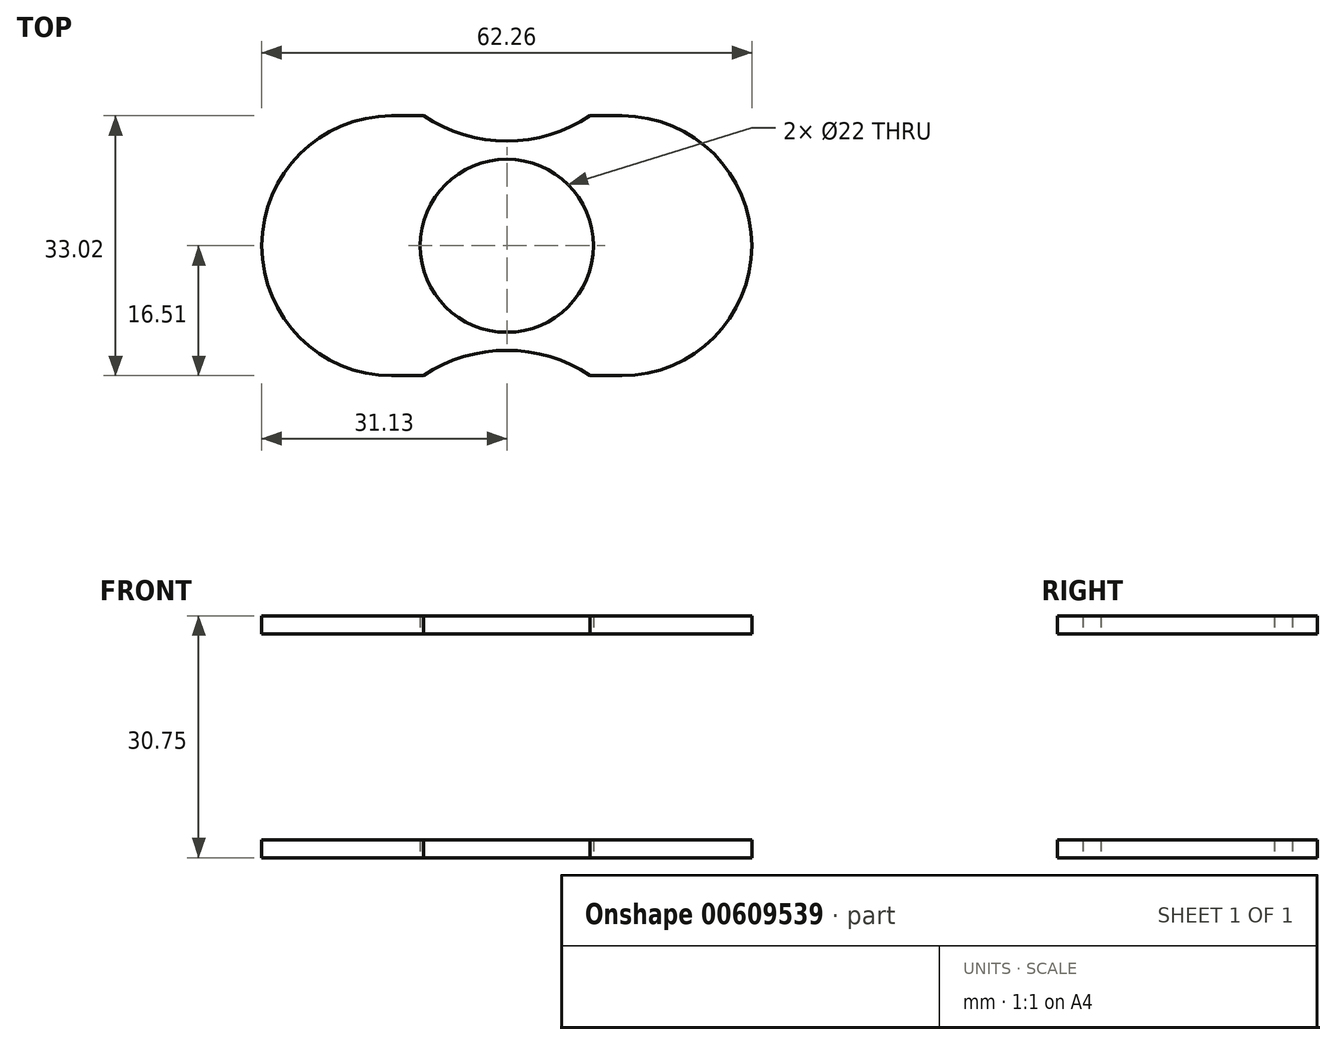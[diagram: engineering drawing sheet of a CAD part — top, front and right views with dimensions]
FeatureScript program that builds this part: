
annotation { "Feature Type Name" : "Feature", "Feature Type Description" : "" }
export const myFeature = defineFeature(function(context is Context, id is Id, definition is map)
    precondition{}
    {
        {
            var Q0;
            Q0=qCreatedBy(makeId("Top.planeOp"),FACE);
            var sketch = newSketch(context, id + "F0", { "sketchPlane" : qUnion([Q0])});
            skLineSegment(sketch, "E0.bottom", {"start": v(27.94, 16.51) * mm, "end": v(-27.94, 16.51) * mm});
            skLineSegment(sketch, "E0.top", {"start": v(27.94, -16.5) * mm, "end": v(-27.94, -16.5) * mm});
            skLineSegment(sketch, "E0.left", {"start": v(27.94, 16.51) * mm, "end": v(27.94, -16.5) * mm});
            skLineSegment(sketch, "E0.right", {"start": v(-27.94, 16.51) * mm, "end": v(-27.94, -16.5) * mm});
            skPoint(sketch, "E0.middle", {"position": v(0, 0) * mm});
            skLineSegment(sketch, "E1", {"start": v(0, 0) * mm, "end": v(0, 32.3) * mm});
            skPoint(sketch, "E1.endSnap0", {"position": v(0, 16.51) * mm});
            skCircle(sketch, "E2", {"center": v(0, 32.3) * mm, "radius": 19 * mm});
            skCircle(sketch, "E3.MirrorC", {"center": v(0, -32.3) * mm, "radius": 19 * mm});
            skLineSegment(sketch, "E4.MirrorCS", {"start": v(0, 0) * mm, "end": v(0, -32.3) * mm});
            skCircle(sketch, "E5", {"center": v(0, 0) * mm, "radius": 11 * mm});
            skArc(sketch, "E6", {"start": v(-14.62, 16.51) * mm, "mid": v(-31.13, 0) * mm, "end": v(-14.62, -16.5) * mm});
            skArc(sketch, "E7.MirrorCS", {"start": v(14.62, 16.51) * mm, "mid": v(31.13, 0) * mm, "end": v(14.62, -16.5) * mm});
            skSolve(sketch);
        }
        {
            var Q0;
            {var subQ13=sQuery(id+"F0.wireOp",EDGE,"b0117b07-4221-4cab-a59d-326007b296140.MirrorCS");Q0=makeQuery(id+"F0.imprint","IMPRINT",FACE,{"disambiguationData":[TD([[makeQuery(id+"F0.imprint","IMPRINT",EDGE,{"derivedFrom":subQ13}),-1.0]])]});}
            var Q1;
            {var subQ0=sQuery(id+"F0.wireOp",EDGE,"6c8b0966-cea6-4925-859d-a13cfbc1d1b40.MirrorCS");Q1=makeQuery(id+"F0.imprint","IMPRINT",FACE,{"disambiguationData":[TD([[makeQuery(id+"F0.imprint","IMPRINT",EDGE,{"derivedFrom":subQ0}),-1.0]])]});}
            var Q2;
            {var subQ0=sQuery(id+"F0.wireOp",EDGE,"xIR9I51y-JtoL-diQV-116K-h4xmKDdJz4Ub");Q2=makeQuery(id+"F0.imprint","IMPRINT",FACE,{"disambiguationData":[TD([[makeQuery(id+"F0.imprint","IMPRINT",EDGE,{"derivedFrom":subQ0}),1.0]])]});}
            var Q3;
            {var subQ0=sQuery(id+"F0.wireOp",EDGE,"UGArh95A-ruyk-S8bi-ieUh-TaEx0mV84ndZ");Q3=makeQuery(id+"F0.imprint","IMPRINT",FACE,{"disambiguationData":[TD([[makeQuery(id+"F0.imprint","IMPRINT",EDGE,{"derivedFrom":subQ0}),-1.0]])]});}
            var Q4;
            {var subQ0=sQuery(id+"F0.wireOp",EDGE,"feb42550-40b8-4ec1-8f83-4ec7968d60970.MirrorCS");Q4=makeQuery(id+"F0.imprint","IMPRINT",FACE,{"disambiguationData":[TD([[makeQuery(id+"F0.imprint","IMPRINT",EDGE,{"derivedFrom":subQ0}),-1.0]])]});}
            var Q5;
            {var subQ0=sQuery(id+"F0.wireOp",EDGE,"6c8b0966-cea6-4925-859d-a13cfbc1d1b40.MirrorCS");Q5=makeQuery(id+"F0.imprint","IMPRINT",FACE,{"disambiguationData":[TD([[makeQuery(id+"F0.imprint","IMPRINT",EDGE,{"derivedFrom":subQ0}),1.0]])]});}
            var Q6;
            {var subQ0=sQuery(id+"F0.wireOp",EDGE,"E6");var subQ9=sQuery(id+"F0.wireOp",EDGE,"E0.bottom");var subQ13=makeQuery(id+"F0.imprint","INTERSECT",VERTEX,{"derivedFrom":[subQ9,subQ0]});Q6=makeQuery(id+"F0.imprint","IMPRINT",FACE,{"disambiguationData":[TD([[makeQuery(id+"F0.imprint","IMPRINT",EDGE,{"disambiguationData":[TD([[subQ13,1.0]])],"derivedFrom":subQ9}),1.0]])]});}
            var Q7;
            {var subQ5=sQuery(id+"F0.wireOp",EDGE,"E7.MirrorCS");var subQ9=sQuery(id+"F0.wireOp",EDGE,"E0.bottom");var subQ10=makeQuery(id+"F0.imprint","INTERSECT",VERTEX,{"derivedFrom":[subQ9,subQ5]});Q7=makeQuery(id+"F0.imprint","IMPRINT",FACE,{"disambiguationData":[TD([[makeQuery(id+"F0.imprint","IMPRINT",EDGE,{"disambiguationData":[TD([[subQ10,-1.0]])],"derivedFrom":subQ9}),1.0]])]});}
            var Q8;
            {var subQ0=sQuery(id+"F0.wireOp",EDGE,"E7.MirrorCS");var subQ1=sQuery(id+"F0.wireOp",EDGE,"E0.left");var subQ2=makeQuery(id+"F0.imprint","INTERSECT",VERTEX,{"disambiguationData":[OD(0.0)],"derivedFrom":[subQ1,subQ0]});Q8=makeQuery(id+"F0.imprint","IMPRINT",FACE,{"disambiguationData":[TD([[makeQuery(id+"F0.imprint","IMPRINT",EDGE,{"disambiguationData":[TD([[subQ2,-1.0]])],"derivedFrom":subQ1}),1.0]])]});}
            var Q9;
            {var subQ0=sQuery(id+"F0.wireOp",EDGE,"E6");var subQ1=sQuery(id+"F0.wireOp",EDGE,"E0.right");var subQ2=makeQuery(id+"F0.imprint","INTERSECT",VERTEX,{"disambiguationData":[OD(0.0)],"derivedFrom":[subQ1,subQ0]});Q9=makeQuery(id+"F0.imprint","IMPRINT",FACE,{"disambiguationData":[TD([[makeQuery(id+"F0.imprint","IMPRINT",EDGE,{"disambiguationData":[TD([[subQ2,-1.0]])],"derivedFrom":subQ1}),-1.0]])]});}
            extrude(context, id + "F1", {"entities" : qUnion([Q0, Q1, Q2, Q3, Q4, Q5, Q6, Q7, Q8, Q9]), "endBound" : BoundingType.SYMMETRIC, "depth" : 2.3 * mm, "offsetDistance" : 25.4 * mm});
        }
        {
            var Q0;
            Q0=makeQuery(id+"F1.opExtrude","SWEPT_BODY",BODY,{"disambiguationData":[OSD([sQuery(id+"F0.wireOp",EDGE,"E0.bottom"),sQuery(id+"F0.wireOp",EDGE,"E0.top"),sQuery(id+"F0.wireOp",EDGE,"E2"),sQuery(id+"F0.wireOp",EDGE,"E3.MirrorC"),sQuery(id+"F0.wireOp",EDGE,"E5"),sQuery(id+"F0.wireOp",EDGE,"E6"),sQuery(id+"F0.wireOp",EDGE,"E7.MirrorCS")])]});
            transform(context, id + "F2", {"entities" : qUnion([Q0]), "transformType" : TransformType.TRANSLATION_3D, "dx" : 0 * mm, "dy" : 0 * mm, "dz" : 28.45 * mm, "makeCopy" : true});
        }
    });
